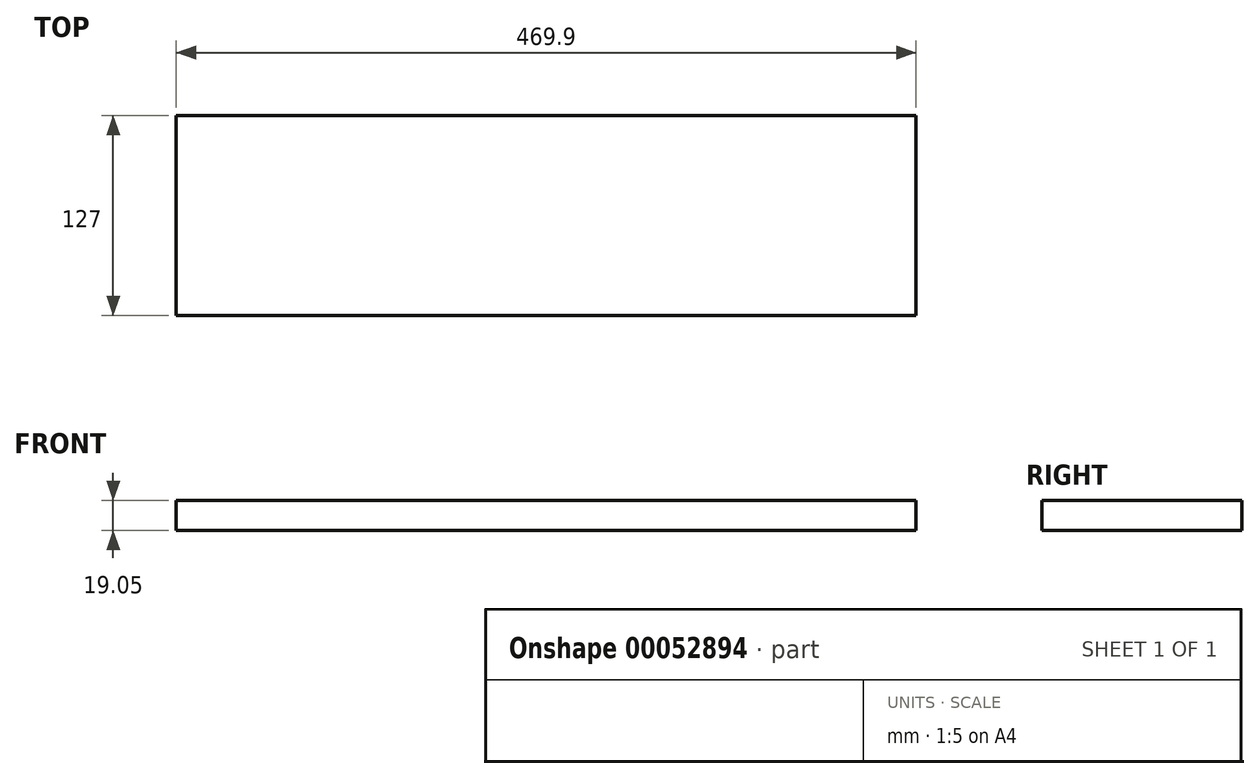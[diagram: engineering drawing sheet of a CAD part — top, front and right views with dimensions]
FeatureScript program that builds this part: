
annotation { "Feature Type Name" : "Feature", "Feature Type Description" : "" }
export const myFeature = defineFeature(function(context is Context, id is Id, definition is map)
    precondition{}
    {
        {
            var Q0;
            Q0=qCreatedBy(makeId("Top.planeOp"),FACE);
            var sketch = newSketch(context, id + "F0", { "sketchPlane" : qUnion([Q0])});
            skLineSegment(sketch, "E0.bottom", {"start": v(0, 0) * mm, "end": v(469.9, 0) * mm});
            skLineSegment(sketch, "E0.top", {"start": v(0, 127) * mm, "end": v(469.9, 127) * mm});
            skLineSegment(sketch, "E0.left", {"start": v(0, 0) * mm, "end": v(0, 127) * mm});
            skLineSegment(sketch, "E0.right", {"start": v(469.9, 0) * mm, "end": v(469.9, 127) * mm});
            skSolve(sketch);
        }
        {
            var Q0;
            Q0 = qSketchRegion(id + "F0", true);
            extrude(context, id + "F1", {"entities" : qUnion([Q0]), "depth" : 19.05 * mm});
        }
    });
